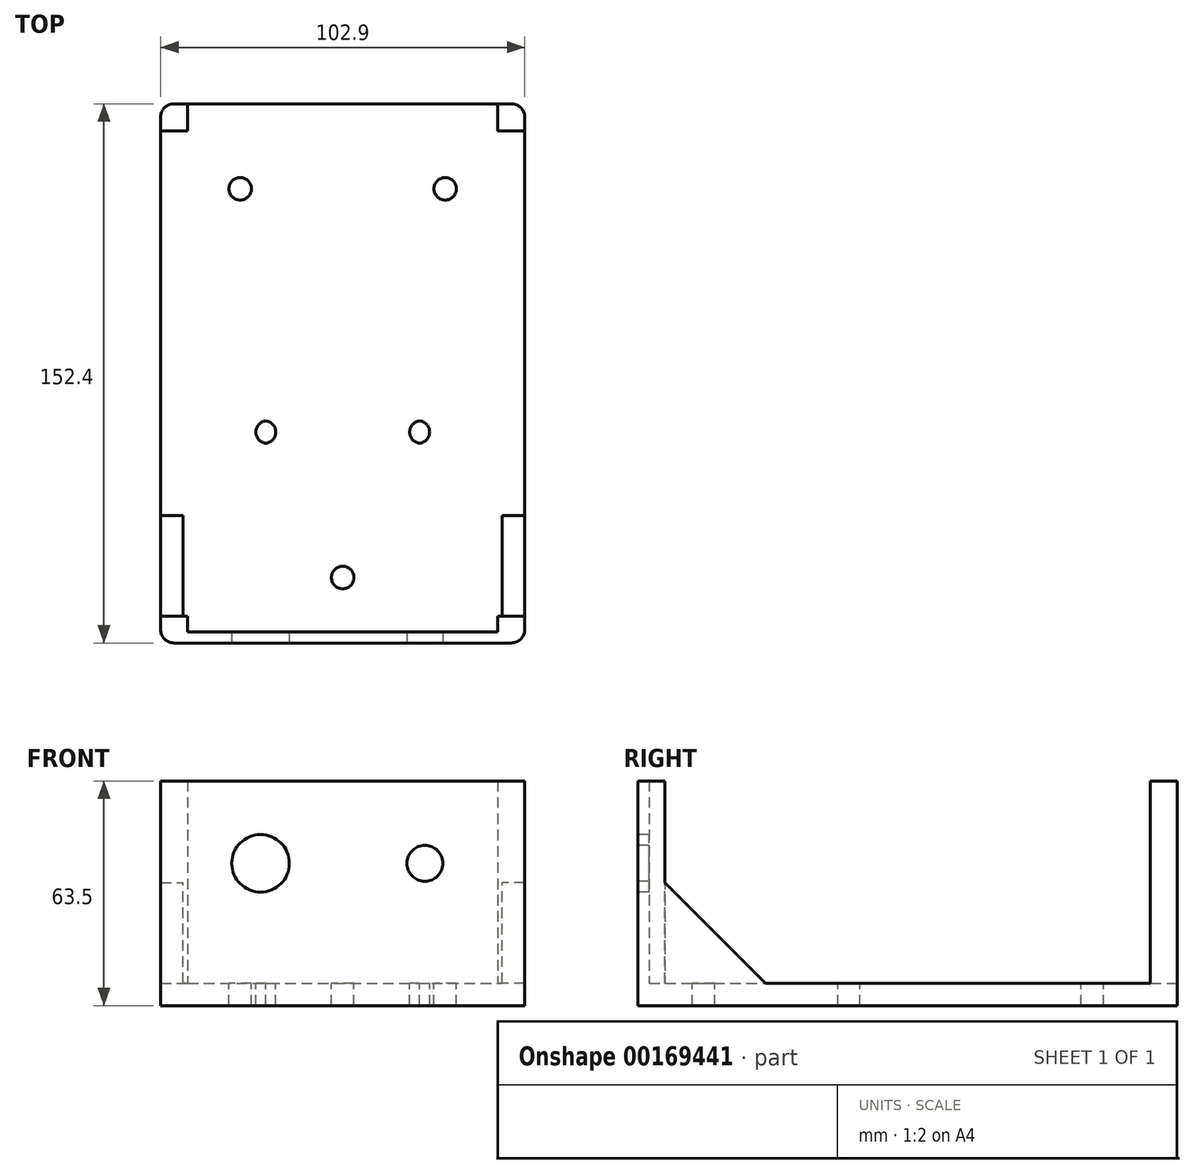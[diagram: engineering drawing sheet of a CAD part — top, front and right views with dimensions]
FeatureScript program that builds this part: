
annotation { "Feature Type Name" : "Feature", "Feature Type Description" : "" }
export const myFeature = defineFeature(function(context is Context, id is Id, definition is map)
    precondition{}
    {
        {
            var Q0;
            Q0=qCreatedBy(makeId("Front.planeOp"),FACE);
            var sketch = newSketch(context, id + "F0", { "sketchPlane" : qUnion([Q0])});
            skLineSegment(sketch, "E0.bottom", {"start": v(-44.45, 23.29) * mm, "end": v(44.45, 23.29) * mm});
            skLineSegment(sketch, "E0.top", {"start": v(-44.45, -40.21) * mm, "end": v(44.45, -40.21) * mm});
            skLineSegment(sketch, "E0.left", {"start": v(-44.45, 23.29) * mm, "end": v(-44.45, -40.21) * mm});
            skLineSegment(sketch, "E0.right", {"start": v(44.45, 23.29) * mm, "end": v(44.45, -40.21) * mm});
            skPoint(sketch, "E0.middle", {"position": v(0, -8.46) * mm});
            skSolve(sketch);
        }
        {
            var Q0;
            Q0=makeQuery(id+"F0.imprint","IMPRINT",FACE,{"disambiguationData":[TD([[makeQuery(id+"F0.imprint","IMPRINT",EDGE,{"derivedFrom":sQuery(id+"F0.wireOp",EDGE,"E0.bottom")}),-1.0]])]});
            extrude(context, id + "F1", {"entities" : qUnion([Q0]), "oppositeDirection" : true, "depth" : 3.17 * mm});
        }
        {
            var Q0;
            Q0=makeQuery(id+"F1.opExtrude","SWEPT_FACE",FACE,{"disambiguationData":[OSD([sQuery(id+"F0.wireOp",EDGE,"E0.top")])]});
            var sketch = newSketch(context, id + "F2", { "sketchPlane" : qUnion([Q0])});
            skLineSegment(sketch, "E1.bottom", {"start": v(44.45, 0) * mm, "end": v(-44.45, 0) * mm});
            skLineSegment(sketch, "E1.top", {"start": v(44.45, -152.4) * mm, "end": v(-44.45, -152.4) * mm});
            skLineSegment(sketch, "E1.left", {"start": v(44.45, 0) * mm, "end": v(44.45, -152.4) * mm});
            skLineSegment(sketch, "E1.right", {"start": v(-44.45, 0) * mm, "end": v(-44.45, -152.4) * mm});
            skSolve(sketch);
        }
        {
            var Q0;
            {var subQ0=sQuery(id+"F2.wireOp",EDGE,"E1.top");Q0=makeQuery(id+"F2.imprint","IMPRINT",FACE,{"disambiguationData":[TD([[makeQuery(id+"F2.imprint","IMPRINT",EDGE,{"derivedFrom":subQ0}),-1.0]])]});}
            extrude(context, id + "F3", {"entities" : qUnion([Q0]), "operationType" : NewBodyOperationType.ADD, "oppositeDirection" : true, "depth" : 6.35 * mm});
        }
        {
            var Q0;
            Q0=makeQuery(id+"F3.boolean.opBoolean","MERGE",FACE,{"derivedFrom":[makeQuery(id+"F1.opExtrude","SWEPT_FACE",FACE,{"disambiguationData":[OSD([sQuery(id+"F0.wireOp",EDGE,"E0.right")])]}),makeQuery(id+"F3.opExtrude","SWEPT_FACE",FACE,{"disambiguationData":[OSD([sQuery(id+"F2.wireOp",EDGE,"E1.left")])]})]});
            var sketch = newSketch(context, id + "F4", { "sketchPlane" : qUnion([Q0])});
            skLineSegment(sketch, "E2.bottom", {"start": v(0, -40.21) * mm, "end": v(38.1, -40.21) * mm});
            skLineSegment(sketch, "E2.top", {"start": v(0, 0) * mm, "end": v(38.1, 0) * mm});
            skLineSegment(sketch, "E2.left", {"start": v(0, -40.21) * mm, "end": v(0, 0) * mm});
            skLineSegment(sketch, "E2.right", {"start": v(38.1, -40.21) * mm, "end": v(38.1, 0) * mm});
            skSolve(sketch);
        }
        {
            var Q0;
            {var subQ0=sQuery(id+"F4.wireOp",EDGE,"E2.right");var subQ1=sQuery(id+"F4.wireOp",EDGE,"E2.top");var subQ2=makeQuery(id+"F4.imprint","INTERSECT",VERTEX,{"derivedFrom":[subQ1,subQ0]});Q0=makeQuery(id+"F4.imprint","IMPRINT",FACE,{"disambiguationData":[TD([[makeQuery(id+"F4.imprint","IMPRINT",EDGE,{"disambiguationData":[TD([[subQ2,1.0]])],"derivedFrom":subQ1}),-1.0]])]});}
            extrude(context, id + "F5", {"entities" : qUnion([Q0]), "operationType" : NewBodyOperationType.ADD, "oppositeDirection" : true, "depth" : 6.35 * mm});
        }
        {
            var Q0;
            Q0=makeQuery(id+"F3.boolean.opBoolean","MERGE",FACE,{"derivedFrom":[makeQuery(id+"F1.opExtrude","SWEPT_FACE",FACE,{"disambiguationData":[OSD([sQuery(id+"F0.wireOp",EDGE,"E0.left")])]}),makeQuery(id+"F3.opExtrude","SWEPT_FACE",FACE,{"disambiguationData":[OSD([sQuery(id+"F2.wireOp",EDGE,"E1.right")])]})]});
            var sketch = newSketch(context, id + "F6", { "sketchPlane" : qUnion([Q0])});
            skLineSegment(sketch, "E3.bottom", {"start": v(0, -40.21) * mm, "end": v(-40.21, -40.21) * mm});
            skLineSegment(sketch, "E3.top", {"start": v(0, 0) * mm, "end": v(-40.21, 0) * mm});
            skLineSegment(sketch, "E3.left", {"start": v(0, -40.21) * mm, "end": v(0, 0) * mm});
            skLineSegment(sketch, "E3.right", {"start": v(-40.21, -40.21) * mm, "end": v(-40.21, 0) * mm});
            skSolve(sketch);
        }
        {
            var Q0;
            {var subQ0=sQuery(id+"F6.wireOp",EDGE,"E3.right");var subQ1=sQuery(id+"F6.wireOp",EDGE,"E3.top");var subQ2=makeQuery(id+"F6.imprint","INTERSECT",VERTEX,{"derivedFrom":[subQ1,subQ0]});Q0=makeQuery(id+"F6.imprint","IMPRINT",FACE,{"disambiguationData":[TD([[makeQuery(id+"F6.imprint","IMPRINT",EDGE,{"disambiguationData":[TD([[subQ2,1.0]])],"derivedFrom":subQ1}),1.0]])]});}
            extrude(context, id + "F7", {"entities" : qUnion([Q0]), "operationType" : NewBodyOperationType.ADD, "oppositeDirection" : true, "depth" : 6.35 * mm});
        }
        {
            var Q0;
            Q0=makeQuery(id+"F7.opExtrude","SWEPT_EDGE",EDGE,{"disambiguationData":[OSD([sQuery(id+"F6.wireOp",EDGE,"E3.top"),sQuery(id+"F6.wireOp",EDGE,"E3.right")])]});
            chamfer(context, id + "F8", {"entities" : qUnion([Q0]), "width" : 38.1 * mm, "tangentPropagation" : true});
        }
        {
            var Q0;
            Q0=makeQuery(id+"F5.opExtrude","SWEPT_EDGE",EDGE,{"disambiguationData":[OSD([sQuery(id+"F4.wireOp",EDGE,"E2.top"),sQuery(id+"F4.wireOp",EDGE,"E2.right")])]});
            chamfer(context, id + "F9", {"entities" : qUnion([Q0]), "width" : 38.1 * mm, "tangentPropagation" : true});
        }
        {
            var Q0;
            Q0=makeQuery(id+"F1.opExtrude","CAP_FACE",FACE,{"disambiguationData":[OSD([sQuery(id+"F0.wireOp",EDGE,"E0.bottom"),sQuery(id+"F0.wireOp",EDGE,"E0.top"),sQuery(id+"F0.wireOp",EDGE,"E0.left"),sQuery(id+"F0.wireOp",EDGE,"E0.right")])],"isStart":true});
            var sketch = newSketch(context, id + "F10", { "sketchPlane" : qUnion([Q0])});
            skCircle(sketch, "E4", {"center": v(-23.48, 0) * mm, "radius": 8 * mm});
            skCircle(sketch, "E5", {"center": v(23.22, 0) * mm, "radius": 5 * mm});
            skSolve(sketch);
        }
        {
            var Q0;
            Q0=makeQuery(id+"F10.imprint","IMPRINT",FACE,{"disambiguationData":[TD([[makeQuery(id+"F10.imprint","IMPRINT",EDGE,{"derivedFrom":sQuery(id+"F10.wireOp",EDGE,"E4")}),1.0]])]});
            extrude(context, id + "F11", {"entities" : qUnion([Q0]), "operationType" : NewBodyOperationType.REMOVE, "endBound" : BoundingType.THROUGH_ALL, "oppositeDirection" : true, "depth" : 25.4 * mm});
        }
        {
            var Q0;
            Q0 = qSketchRegion(id + "F10", true);
            extrude(context, id + "F12", {"entities" : qUnion([Q0]), "operationType" : NewBodyOperationType.REMOVE, "oppositeDirection" : true, "depth" : 25.4 * mm});
        }
        {
            var Q0;
            Q0=makeQuery(id+"F3.opExtrude","CAP_FACE",FACE,{"disambiguationData":[OSD([sQuery(id+"F0.wireOp",EDGE,"E0.top"),sQuery(id+"F2.wireOp",EDGE,"E1.top"),sQuery(id+"F2.wireOp",EDGE,"E1.left"),sQuery(id+"F2.wireOp",EDGE,"E1.right")])],"isStart":false});
            var sketch = newSketch(context, id + "F13", { "sketchPlane" : qUnion([Q0])});
            skCircle(sketch, "E6", {"center": v(0, 18.5) * mm, "radius": 3.18 * mm});
            skCircle(sketch, "E7", {"center": v(-22.08, 59.6) * mm, "radius": 3.18 * mm});
            skCircle(sketch, "E8", {"center": v(21.37, 59.6) * mm, "radius": 3.18 * mm});
            skSolve(sketch);
        }
        {
            var Q0;
            Q0 = qSketchRegion(id + "F13", true);
            extrude(context, id + "F14", {"entities" : qUnion([Q0]), "operationType" : NewBodyOperationType.REMOVE, "oppositeDirection" : true, "depth" : 25.4 * mm});
        }
        {
            var Q0;
            {var subQ0=sQuery(id+"F2.wireOp",EDGE,"E1.left");var subQ1=sQuery(id+"F0.wireOp",EDGE,"E0.right");Q0=makeQuery(id+"F5.boolean.opBoolean","MERGE",FACE,{"derivedFrom":[makeQuery(id+"F3.boolean.opBoolean","MERGE",FACE,{"derivedFrom":[makeQuery(id+"F1.opExtrude","SWEPT_FACE",FACE,{"disambiguationData":[OSD([subQ1])]}),makeQuery(id+"F3.opExtrude","SWEPT_FACE",FACE,{"disambiguationData":[OSD([subQ0])]})]}),makeQuery(id+"F5.opExtrude","CAP_FACE",FACE,{"disambiguationData":[OSD([subQ1,subQ0,sQuery(id+"F4.wireOp",EDGE,"E2.top"),sQuery(id+"F4.wireOp",EDGE,"E2.right")])],"isStart":true})]});}
            extrude(context, id + "F15", {"entities" : qUnion([Q0]), "operationType" : NewBodyOperationType.ADD, "depth" : 7 * mm});
        }
        {
            var Q0;
            {var subQ0=sQuery(id+"F2.wireOp",EDGE,"E1.right");var subQ1=sQuery(id+"F0.wireOp",EDGE,"E0.left");Q0=makeQuery(id+"F7.boolean.opBoolean","MERGE",FACE,{"derivedFrom":[makeQuery(id+"F3.boolean.opBoolean","MERGE",FACE,{"derivedFrom":[makeQuery(id+"F1.opExtrude","SWEPT_FACE",FACE,{"disambiguationData":[OSD([subQ1])]}),makeQuery(id+"F3.opExtrude","SWEPT_FACE",FACE,{"disambiguationData":[OSD([subQ0])]})]}),makeQuery(id+"F7.opExtrude","CAP_FACE",FACE,{"disambiguationData":[OSD([subQ1,subQ0,sQuery(id+"F6.wireOp",EDGE,"E3.top"),sQuery(id+"F6.wireOp",EDGE,"E3.right")])],"isStart":true})]});}
            extrude(context, id + "F16", {"entities" : qUnion([Q0]), "operationType" : NewBodyOperationType.ADD, "depth" : 7 * mm});
        }
        {
            var Q0;
            Q0=makeQuery(id+"F5.opExtrude","CAP_FACE",FACE,{"disambiguationData":[OSD([sQuery(id+"F0.wireOp",EDGE,"E0.right"),sQuery(id+"F2.wireOp",EDGE,"E1.left"),sQuery(id+"F4.wireOp",EDGE,"E2.top"),sQuery(id+"F4.wireOp",EDGE,"E2.right")])],"isStart":false});
            extrude(context, id + "F17", {"entities" : qUnion([Q0]), "operationType" : NewBodyOperationType.REMOVE, "oppositeDirection" : true, "depth" : 7 * mm});
        }
        {
            var Q0;
            Q0=makeQuery(id+"F7.opExtrude","CAP_FACE",FACE,{"disambiguationData":[OSD([sQuery(id+"F0.wireOp",EDGE,"E0.left"),sQuery(id+"F2.wireOp",EDGE,"E1.right"),sQuery(id+"F6.wireOp",EDGE,"E3.top"),sQuery(id+"F6.wireOp",EDGE,"E3.right")])],"isStart":false});
            extrude(context, id + "F18", {"entities" : qUnion([Q0]), "operationType" : NewBodyOperationType.REMOVE, "oppositeDirection" : true, "depth" : 7 * mm});
        }
        {
            var Q0;
            {var subQ0=sQuery(id+"F2.wireOp",EDGE,"E1.right");var subQ1=sQuery(id+"F0.wireOp",EDGE,"E0.top");var subQ2=sQuery(id+"F2.wireOp",EDGE,"E1.left");Q0=makeQuery(id+"F16.boolean.opBoolean","MERGE",FACE,{"derivedFrom":[makeQuery(id+"F15.boolean.opBoolean","MERGE",FACE,{"derivedFrom":[makeQuery(id+"F3.boolean.opBoolean","MERGE",FACE,{"derivedFrom":[makeQuery(id+"F1.opExtrude","SWEPT_FACE",FACE,{"disambiguationData":[OSD([subQ1])]}),makeQuery(id+"F3.opExtrude","CAP_FACE",FACE,{"disambiguationData":[OSD([subQ1,sQuery(id+"F2.wireOp",EDGE,"E1.top"),subQ2,subQ0])],"isStart":true})]}),makeQuery(id+"F15.opExtrude","SWEPT_FACE",FACE,{"disambiguationData":[OSD([subQ1,sQuery(id+"F0.wireOp",EDGE,"E0.right"),subQ2])]})]}),makeQuery(id+"F16.opExtrude","SWEPT_FACE",FACE,{"disambiguationData":[OSD([subQ1,sQuery(id+"F0.wireOp",EDGE,"E0.left"),subQ0])]})]});}
            var sketch = newSketch(context, id + "F19", { "sketchPlane" : qUnion([Q0])});
            skLineSegment(sketch, "E9.bottom", {"start": v(51.45, -144.78) * mm, "end": v(43.83, -144.78) * mm});
            skLineSegment(sketch, "E9.top", {"start": v(51.45, -152.4) * mm, "end": v(43.83, -152.4) * mm});
            skLineSegment(sketch, "E9.left", {"start": v(51.45, -144.78) * mm, "end": v(51.45, -152.4) * mm});
            skLineSegment(sketch, "E9.right", {"start": v(43.83, -144.78) * mm, "end": v(43.83, -152.4) * mm});
            skSolve(sketch);
        }
        {
            var Q0;
            Q0=makeQuery(id+"F19.imprint","IMPRINT",FACE,{"disambiguationData":[TD([[makeQuery(id+"F19.imprint","IMPRINT",EDGE,{"derivedFrom":sQuery(id+"F19.wireOp",EDGE,"E9.bottom")}),1.0]])]});
            extrude(context, id + "F20", {"entities" : qUnion([Q0]), "operationType" : NewBodyOperationType.ADD, "oppositeDirection" : true, "depth" : 63.5 * mm});
        }
        {
            var Q0;
            {var subQ0=sQuery(id+"F0.wireOp",EDGE,"E0.left");var subQ1=sQuery(id+"F0.wireOp",EDGE,"E0.right");var subQ2=makeQuery(id+"F16.boolean.opBoolean","MERGE",FACE,{"derivedFrom":[makeQuery(id+"F15.boolean.opBoolean","MERGE",FACE,{"derivedFrom":[makeQuery(id+"F1.opExtrude","CAP_FACE",FACE,{"disambiguationData":[OSD([sQuery(id+"F0.wireOp",EDGE,"E0.bottom"),sQuery(id+"F0.wireOp",EDGE,"E0.top"),subQ0,subQ1])],"isStart":true}),makeQuery(id+"F15.opExtrude","SWEPT_FACE",FACE,{"disambiguationData":[OSD([subQ1]),TDD([makeQuery(id+"F1.opExtrude","CAP_EDGE",EDGE,{"disambiguationData":[OSD([subQ1])],"isStart":true})])]})]}),makeQuery(id+"F16.opExtrude","SWEPT_FACE",FACE,{"disambiguationData":[OSD([subQ0]),TDD([makeQuery(id+"F1.opExtrude","CAP_EDGE",EDGE,{"disambiguationData":[OSD([subQ0])],"isStart":true})])]})]});Q0=makeQuery(id+"FNemScOIYdZmHjy_1.boolean.opBoolean","MERGE",FACE,{"derivedFrom":[subQ2,makeQuery(id+"FNemScOIYdZmHjy_1.opPattern","COPY",FACE,{"derivedFrom":subQ2,"instanceName":"1"})]});}
            var sketch = newSketch(context, id + "F21", { "sketchPlane" : qUnion([Q0])});
            skLineSegment(sketch, "E10.bottom", {"start": v(-51.45, 23.29) * mm, "end": v(-43.83, 23.29) * mm});
            skLineSegment(sketch, "E10.top", {"start": v(-51.45, -40.21) * mm, "end": v(-43.83, -40.21) * mm});
            skLineSegment(sketch, "E10.left", {"start": v(-51.45, 23.29) * mm, "end": v(-51.45, -40.21) * mm});
            skLineSegment(sketch, "E10.right", {"start": v(-43.83, 23.29) * mm, "end": v(-43.83, -40.21) * mm});
            skSolve(sketch);
        }
        {
            var Q0;
            Q0 = qSketchRegion(id + "F21", true);
            extrude(context, id + "F22", {"entities" : qUnion([Q0]), "operationType" : NewBodyOperationType.ADD, "oppositeDirection" : true, "depth" : 7.62 * mm});
        }
        {
            var Q0;
            Q0=makeQuery(id+"F1.opExtrude","SWEPT_BODY",BODY,{"disambiguationData":[OSD([sQuery(id+"F0.wireOp",EDGE,"E0.bottom"),sQuery(id+"F0.wireOp",EDGE,"E0.top"),sQuery(id+"F0.wireOp",EDGE,"E0.left"),sQuery(id+"F0.wireOp",EDGE,"E0.right")])]});
            var Q1;
            Q1=qCreatedBy(makeId("Right.planeOp"),FACE);
            mirror(context, id + "F23", {"operationType" : NewBodyOperationType.ADD, "entities" : qUnion([Q0]), "mirrorPlane" : qUnion([Q1])});
        }
        {
            var Q0;
            {var subQ0=sQuery(id+"F0.wireOp",EDGE,"E0.right");Q0=makeQuery(id+"F15.opExtrude","CAP_EDGE",EDGE,{"disambiguationData":[OSD([subQ0]),TDD([makeQuery(id+"F1.opExtrude","CAP_EDGE",EDGE,{"disambiguationData":[OSD([subQ0])],"isStart":true})])],"isStart":false});}
            fillet(context, id + "F24", {"entities" : qUnion([Q0]), "radius" : 3.8 * mm, "tangentPropagation" : true, "allowEdgeOverflow" : false});
        }
        {
            var Q0;
            {var subQ0=sQuery(id+"F0.wireOp",EDGE,"E0.left");Q0=makeQuery(id+"F16.opExtrude","CAP_EDGE",EDGE,{"disambiguationData":[OSD([subQ0]),TDD([makeQuery(id+"F1.opExtrude","CAP_EDGE",EDGE,{"disambiguationData":[OSD([subQ0])],"isStart":true})])],"isStart":false});}
            fillet(context, id + "F25", {"entities" : qUnion([Q0]), "radius" : 3.8 * mm, "tangentPropagation" : true, "allowEdgeOverflow" : false});
        }
        {
            var Q0;
            {var subQ0=sQuery(id+"F2.wireOp",EDGE,"E1.top");Q0=makeQuery(id+"FNemScOIYdZmHjy_1.boolean.opBoolean","MERGE",EDGE,{"derivedFrom":[makeQuery(id+"F16.opExtrude","CAP_EDGE",EDGE,{"disambiguationData":[OSD([subQ0,sQuery(id+"F2.wireOp",EDGE,"E1.right")])],"isStart":false}),makeQuery(id+"FNemScOIYdZmHjy_1.opPattern","COPY",EDGE,{"derivedFrom":makeQuery(id+"F20.boolean.opBoolean","MERGE",EDGE,{"derivedFrom":[makeQuery(id+"F15.opExtrude","CAP_EDGE",EDGE,{"disambiguationData":[OSD([subQ0,sQuery(id+"F2.wireOp",EDGE,"E1.left")])],"isStart":false}),makeQuery(id+"F20.opExtrude","SWEPT_EDGE",EDGE,{"disambiguationData":[OSD([sQuery(id+"F19.wireOp",EDGE,"E9.top"),sQuery(id+"F19.wireOp",EDGE,"E9.left")])]})]}),"instanceName":"1"})]});}
            fillet(context, id + "F26", {"entities" : qUnion([Q0]), "radius" : 3.8 * mm, "tangentPropagation" : true, "allowEdgeOverflow" : false});
        }
        {
            var Q0;
            Q0=makeQuery(id+"F20.boolean.opBoolean","MERGE",EDGE,{"derivedFrom":[makeQuery(id+"F15.opExtrude","CAP_EDGE",EDGE,{"disambiguationData":[OSD([sQuery(id+"F2.wireOp",EDGE,"E1.top"),sQuery(id+"F2.wireOp",EDGE,"E1.left")])],"isStart":false}),makeQuery(id+"F20.opExtrude","SWEPT_EDGE",EDGE,{"disambiguationData":[OSD([sQuery(id+"F19.wireOp",EDGE,"E9.top"),sQuery(id+"F19.wireOp",EDGE,"E9.left")])]})]});
            fillet(context, id + "F27", {"entities" : qUnion([Q0]), "radius" : 3.8 * mm, "tangentPropagation" : true, "allowEdgeOverflow" : false});
        }
        {
            var Q0;
            Q0=makeQuery(id+"F13.imprint","IMPRINT",FACE,{"disambiguationData":[TD([[makeQuery(id+"F13.imprint","IMPRINT",EDGE,{"derivedFrom":sQuery(id+"F13.wireOp",EDGE,"E6")}),-1.0]])]});
            var sketch = newSketch(context, id + "F28", { "sketchPlane" : qUnion([Q0])});
            skCircle(sketch, "E11", {"center": v(28.97, 128.38) * mm, "radius": 3.18 * mm});
            skCircle(sketch, "E12.MirrorC", {"center": v(-28.97, 128.38) * mm, "radius": 3.18 * mm});
            skSolve(sketch);
        }
        {
            var Q0;
            Q0 = qSketchRegion(id + "F28", true);
            extrude(context, id + "F29", {"entities" : qUnion([Q0]), "operationType" : NewBodyOperationType.REMOVE, "oppositeDirection" : true, "depth" : 25.4 * mm});
        }
        {
            var Q0;
            {var subQ0=sQuery(id+"F0.wireOp",EDGE,"E0.left");var subQ1=sQuery(id+"F0.wireOp",EDGE,"E0.right");var subQ2=makeQuery(id+"F16.boolean.opBoolean","MERGE",FACE,{"derivedFrom":[makeQuery(id+"F15.boolean.opBoolean","MERGE",FACE,{"derivedFrom":[makeQuery(id+"F1.opExtrude","CAP_FACE",FACE,{"disambiguationData":[OSD([sQuery(id+"F0.wireOp",EDGE,"E0.bottom"),sQuery(id+"F0.wireOp",EDGE,"E0.top"),subQ0,subQ1])],"isStart":true}),makeQuery(id+"F15.opExtrude","SWEPT_FACE",FACE,{"disambiguationData":[OSD([subQ1]),TDD([makeQuery(id+"F1.opExtrude","CAP_EDGE",EDGE,{"disambiguationData":[OSD([subQ1])],"isStart":true})])]})]}),makeQuery(id+"F16.opExtrude","SWEPT_FACE",FACE,{"disambiguationData":[OSD([subQ0]),TDD([makeQuery(id+"F1.opExtrude","CAP_EDGE",EDGE,{"disambiguationData":[OSD([subQ0])],"isStart":true})])]})]});Q0=makeQuery(id+"F23.boolean.opBoolean","MERGE",FACE,{"derivedFrom":[subQ2,makeQuery(id+"F23.opPattern","COPY",FACE,{"derivedFrom":subQ2,"instanceName":"1"})]});}
            var sketch = newSketch(context, id + "F30", { "sketchPlane" : qUnion([Q0])});
            skCircle(sketch, "E13", {"center": v(-23.22, 0) * mm, "radius": 8.13 * mm});
            skSolve(sketch);
        }
        {
            var Q0;
            Q0 = qSketchRegion(id + "F30", true);
            extrude(context, id + "F31", {"entities" : qUnion([Q0]), "operationType" : NewBodyOperationType.REMOVE, "oppositeDirection" : true, "depth" : 25.4 * mm});
        }
        {
            var Q0;
            {var subQ0=sQuery(id+"F0.wireOp",EDGE,"E0.left");var subQ1=sQuery(id+"F0.wireOp",EDGE,"E0.right");var subQ2=makeQuery(id+"F16.boolean.opBoolean","MERGE",FACE,{"derivedFrom":[makeQuery(id+"F15.boolean.opBoolean","MERGE",FACE,{"derivedFrom":[makeQuery(id+"F1.opExtrude","CAP_FACE",FACE,{"disambiguationData":[OSD([sQuery(id+"F0.wireOp",EDGE,"E0.bottom"),sQuery(id+"F0.wireOp",EDGE,"E0.top"),subQ0,subQ1])],"isStart":true}),makeQuery(id+"F15.opExtrude","SWEPT_FACE",FACE,{"disambiguationData":[OSD([subQ1]),TDD([makeQuery(id+"F1.opExtrude","CAP_EDGE",EDGE,{"disambiguationData":[OSD([subQ1])],"isStart":true})])]})]}),makeQuery(id+"F16.opExtrude","SWEPT_FACE",FACE,{"disambiguationData":[OSD([subQ0]),TDD([makeQuery(id+"F1.opExtrude","CAP_EDGE",EDGE,{"disambiguationData":[OSD([subQ0])],"isStart":true})])]})]});Q0=makeQuery(id+"F23.boolean.opBoolean","MERGE",FACE,{"derivedFrom":[subQ2,makeQuery(id+"F23.opPattern","COPY",FACE,{"derivedFrom":subQ2,"instanceName":"1"})]});}
            var sketch = newSketch(context, id + "F32", { "sketchPlane" : qUnion([Q0])});
            skCircle(sketch, "E14", {"center": v(23.22, 0) * mm, "radius": 5.08 * mm});
            skSolve(sketch);
        }
        {
            var Q0;
            Q0 = qSketchRegion(id + "F32", true);
            extrude(context, id + "F33", {"entities" : qUnion([Q0]), "operationType" : NewBodyOperationType.REMOVE, "oppositeDirection" : true, "depth" : 25.4 * mm});
        }
    });
